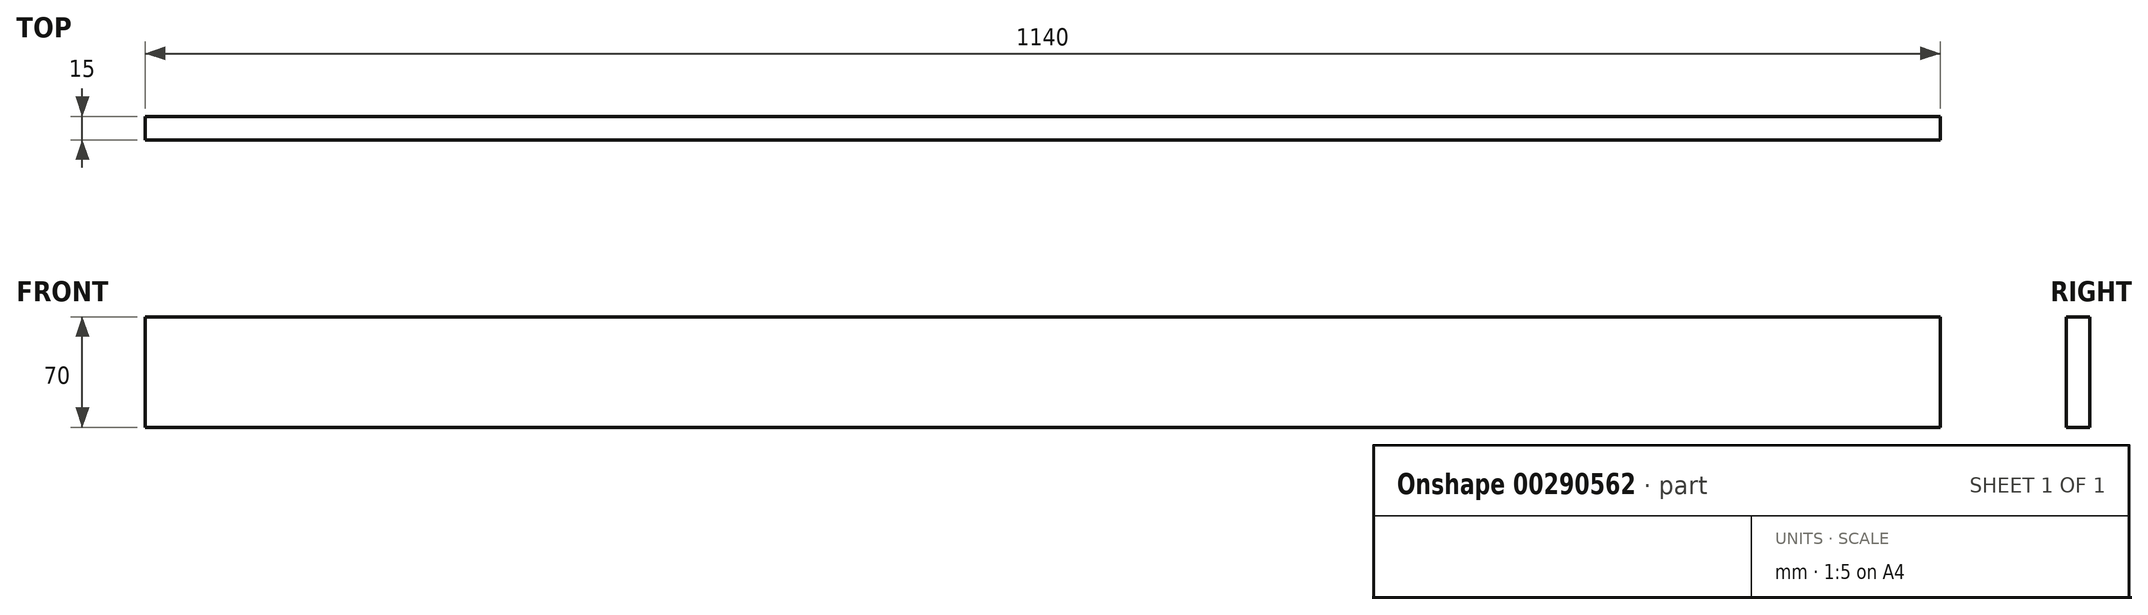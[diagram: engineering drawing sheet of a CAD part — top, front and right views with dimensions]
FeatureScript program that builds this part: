
annotation { "Feature Type Name" : "Feature", "Feature Type Description" : "" }
export const myFeature = defineFeature(function(context is Context, id is Id, definition is map)
    precondition{}
    {
        {
            var Q0;
            Q0=qCreatedBy(makeId("Right.planeOp"),FACE);
            var sketch = newSketch(context, id + "F0", { "sketchPlane" : qUnion([Q0])});
            skLineSegment(sketch, "E0.bottom", {"start": v(0, 0) * mm, "end": v(-15, 0) * mm});
            skLineSegment(sketch, "E0.top", {"start": v(0, 70) * mm, "end": v(-15, 70) * mm});
            skLineSegment(sketch, "E0.left", {"start": v(0, 0) * mm, "end": v(0, 70) * mm});
            skLineSegment(sketch, "E0.right", {"start": v(-15, 0) * mm, "end": v(-15, 70) * mm});
            skSolve(sketch);
        }
        {
            var Q0;
            Q0=makeQuery(id+"F0.imprint","IMPRINT",FACE,{"disambiguationData":[TD([[makeQuery(id+"F0.imprint","IMPRINT",EDGE,{"derivedFrom":sQuery(id+"F0.wireOp",EDGE,"E0.bottom")}),-1.0]])]});
            extrude(context, id + "F1", {"entities" : qUnion([Q0]), "depth" : 1140 * mm});
        }
    });
